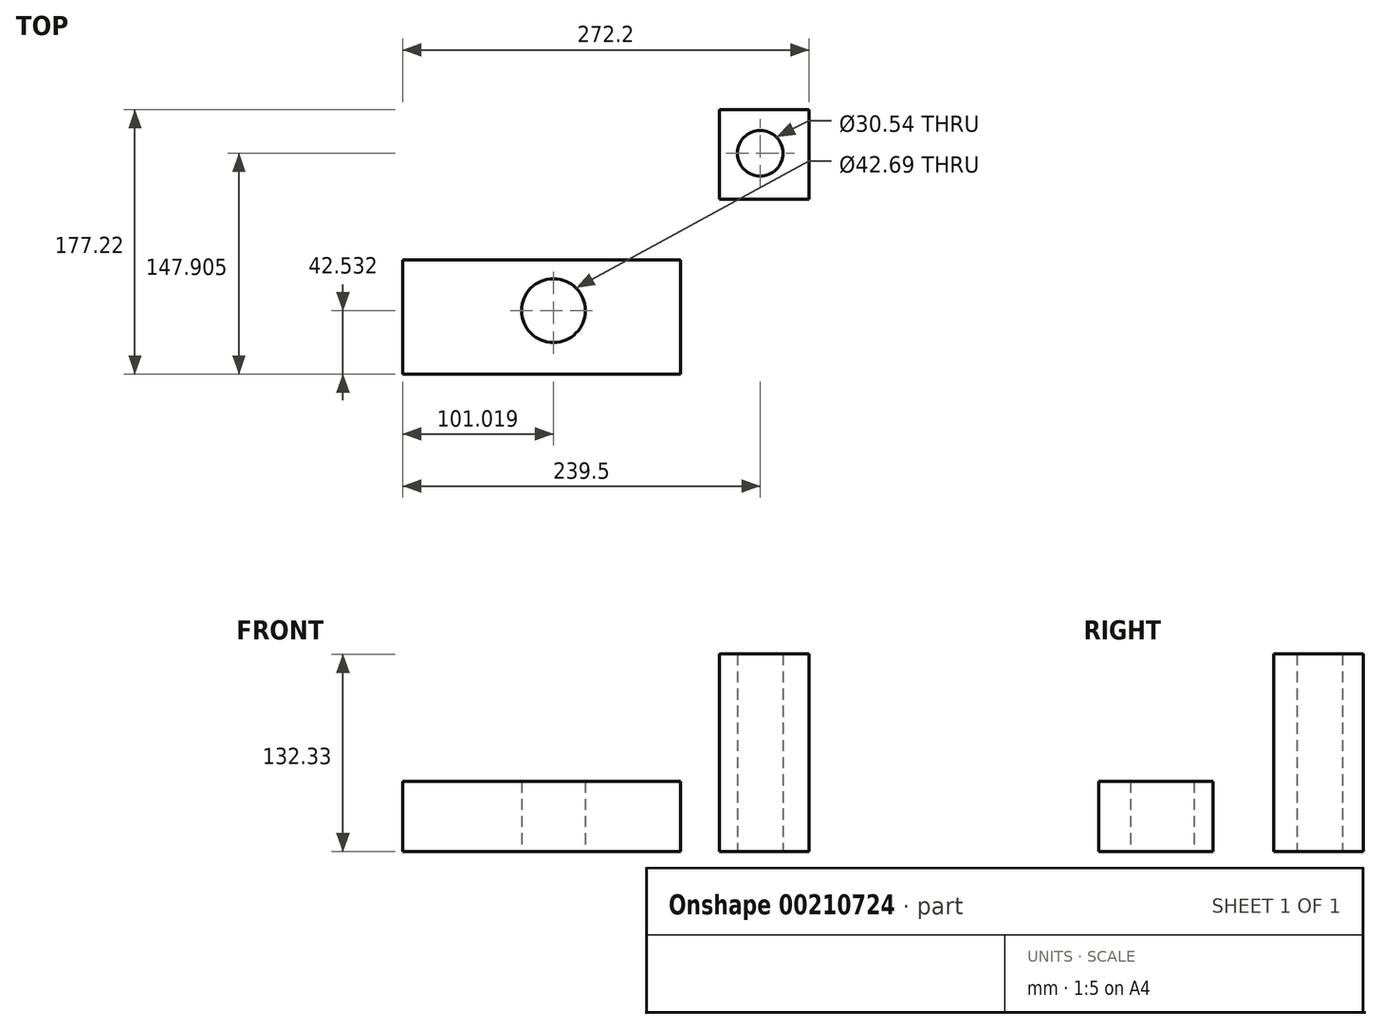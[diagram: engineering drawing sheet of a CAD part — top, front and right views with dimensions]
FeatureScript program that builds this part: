
annotation { "Feature Type Name" : "Feature", "Feature Type Description" : "" }
export const myFeature = defineFeature(function(context is Context, id is Id, definition is map)
    precondition{}
    {
        {
            var Q0;
            Q0=qCreatedBy(makeId("Top.planeOp"),FACE);
            var sketch = newSketch(context, id + "F0", { "sketchPlane" : qUnion([Q0])});
            skLineSegment(sketch, "E0.bottom", {"start": v(0, 0) * mm, "end": v(-93, 0) * mm});
            skLineSegment(sketch, "E0.top", {"start": v(0, -76.62) * mm, "end": v(-93, -76.62) * mm});
            skLineSegment(sketch, "E0.left", {"start": v(0, 0) * mm, "end": v(0, -76.62) * mm});
            skLineSegment(sketch, "E0.right", {"start": v(-93, 0) * mm, "end": v(-93, -76.62) * mm});
            skCircle(sketch, "E1", {"center": v(-50.91, -34.09) * mm, "radius": 21.34 * mm});
            skSolve(sketch);
        }
        {
            var Q0;
            Q0 = qSketchRegion(id + "F0", true);
            extrude(context, id + "F1", {"entities" : qUnion([Q0]), "depth" : 47 * mm});
        }
        {
            var Q0;
            Q0=makeQuery(id+"F1.opExtrude","SWEPT_FACE",FACE,{"disambiguationData":[OSD([sQuery(id+"F0.wireOp",EDGE,"E0.left")])]});
            extrude(context, id + "F2", {"entities" : qUnion([Q0]), "operationType" : NewBodyOperationType.ADD, "depth" : 34.3 * mm});
        }
        {
            var Q0;
            Q0=makeQuery(id+"F1.opExtrude","SWEPT_FACE",FACE,{"disambiguationData":[OSD([sQuery(id+"F0.wireOp",EDGE,"E0.right")])]});
            extrude(context, id + "F3", {"entities" : qUnion([Q0]), "operationType" : NewBodyOperationType.ADD, "depth" : 58.93 * mm});
        }
        {
            var Q0;
            Q0=qCreatedBy(makeId("Top.planeOp"),FACE);
            var sketch = newSketch(context, id + "F4", { "sketchPlane" : qUnion([Q0])});
            skLineSegment(sketch, "E2.bottom", {"start": v(60.27, 40.6) * mm, "end": v(120.27, 40.6) * mm});
            skLineSegment(sketch, "E2.top", {"start": v(60.27, 100.6) * mm, "end": v(120.27, 100.6) * mm});
            skLineSegment(sketch, "E2.left", {"start": v(60.27, 40.6) * mm, "end": v(60.27, 100.6) * mm});
            skLineSegment(sketch, "E2.right", {"start": v(120.27, 40.6) * mm, "end": v(120.27, 100.6) * mm});
            skCircle(sketch, "E3", {"center": v(87.57, 71.28) * mm, "radius": 15.27 * mm});
            skSolve(sketch);
        }
        {
            var Q0;
            Q0=makeQuery(id+"F4.imprint","IMPRINT",FACE,{"disambiguationData":[TD([[makeQuery(id+"F4.imprint","IMPRINT",EDGE,{"derivedFrom":sQuery(id+"F4.wireOp",EDGE,"E2.bottom")}),1.0]])]});
            extrude(context, id + "F5", {"entities" : qUnion([Q0]), "depth" : 132.33 * mm});
        }
    });
